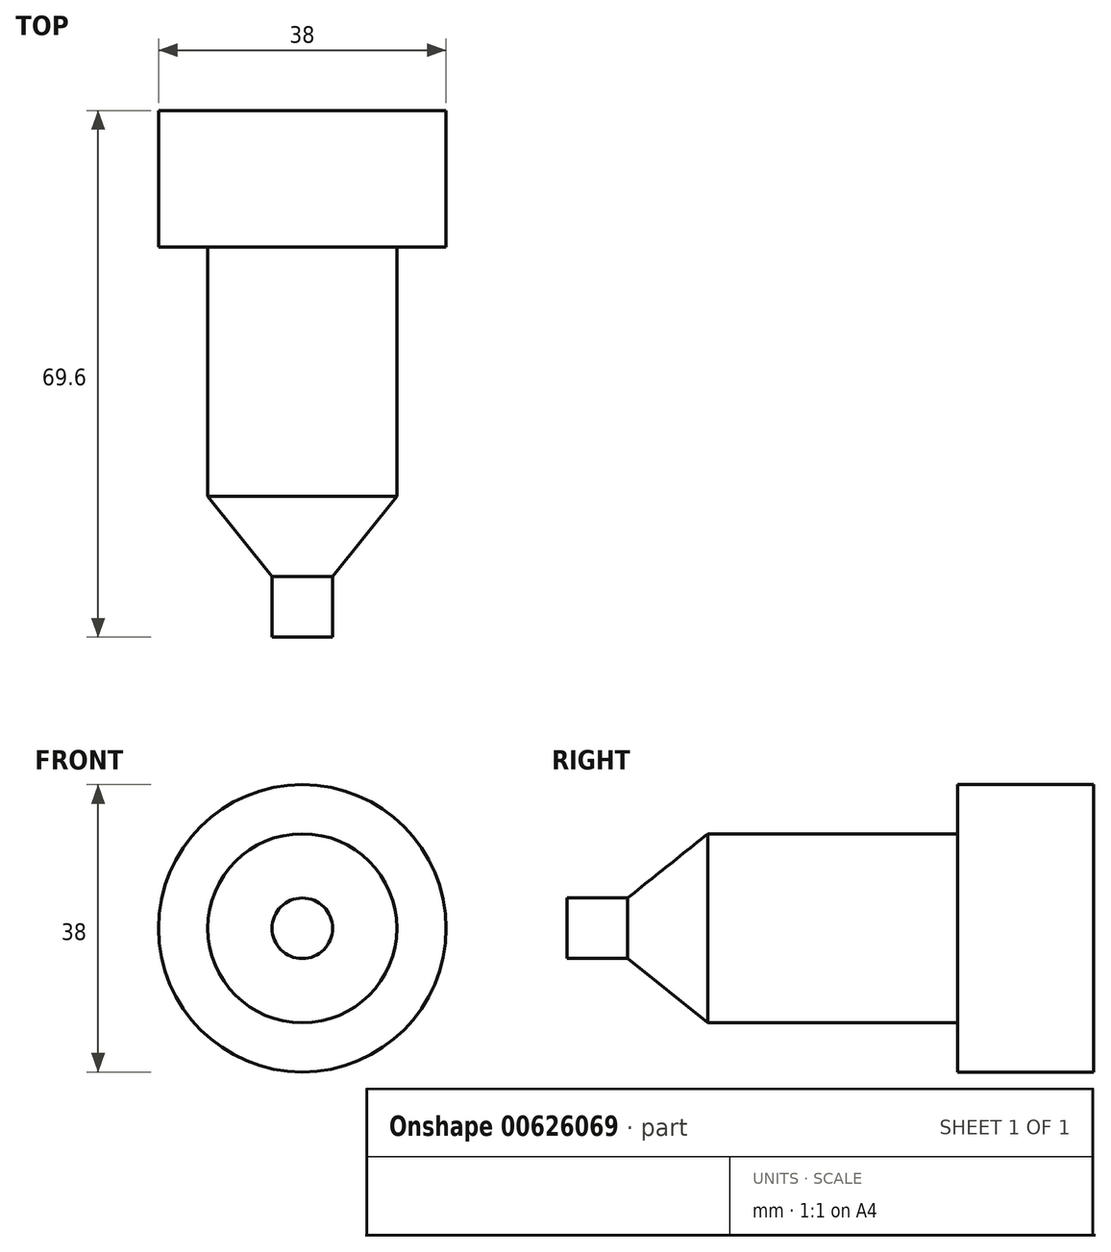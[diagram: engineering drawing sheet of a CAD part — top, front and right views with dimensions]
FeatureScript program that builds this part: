
annotation { "Feature Type Name" : "Feature", "Feature Type Description" : "" }
export const myFeature = defineFeature(function(context is Context, id is Id, definition is map)
    precondition{}
    {
        {
            var Q0;
            Q0=qCreatedBy(makeId("Right.planeOp"),FACE);
            var sketch = newSketch(context, id + "F0", { "sketchPlane" : qUnion([Q0])});
            skLineSegment(sketch, "E0", {"start": v(-69.6, 4) * mm, "end": v(-61.6, 4) * mm});
            skLineSegment(sketch, "E1", {"start": v(-61.6, 4) * mm, "end": v(-51, 12.5) * mm});
            skLineSegment(sketch, "E2", {"start": v(-51, 12.5) * mm, "end": v(-18, 12.5) * mm});
            skLineSegment(sketch, "E3", {"start": v(-18, 12.5) * mm, "end": v(-18, 19) * mm});
            skLineSegment(sketch, "E4", {"start": v(-18, 19) * mm, "end": v(0, 19) * mm});
            skLineSegment(sketch, "E5", {"start": v(0, 19) * mm, "end": v(0, 0) * mm});
            skLineSegment(sketch, "E6", {"start": v(0, 0) * mm, "end": v(-69.6, 0) * mm});
            skLineSegment(sketch, "E7", {"start": v(-69.6, 4) * mm, "end": v(-69.6, 0) * mm});
            skSolve(sketch);
        }
        {
            var Q0;
            Q0=makeQuery(id+"F0.imprint","IMPRINT",FACE,{"disambiguationData":[TD([[makeQuery(id+"F0.imprint","IMPRINT",EDGE,{"derivedFrom":sQuery(id+"F0.wireOp",EDGE,"E0")}),-1.0]])]});
            var Q1;
            Q1=sQuery(id+"F0.wireOp",EDGE,"E6");
            revolve(context, id + "F1", {"entities" : qUnion([Q0]), "axis" : qUnion([Q1]), "revolveType" : RevolveType.FULL});
        }
    });
